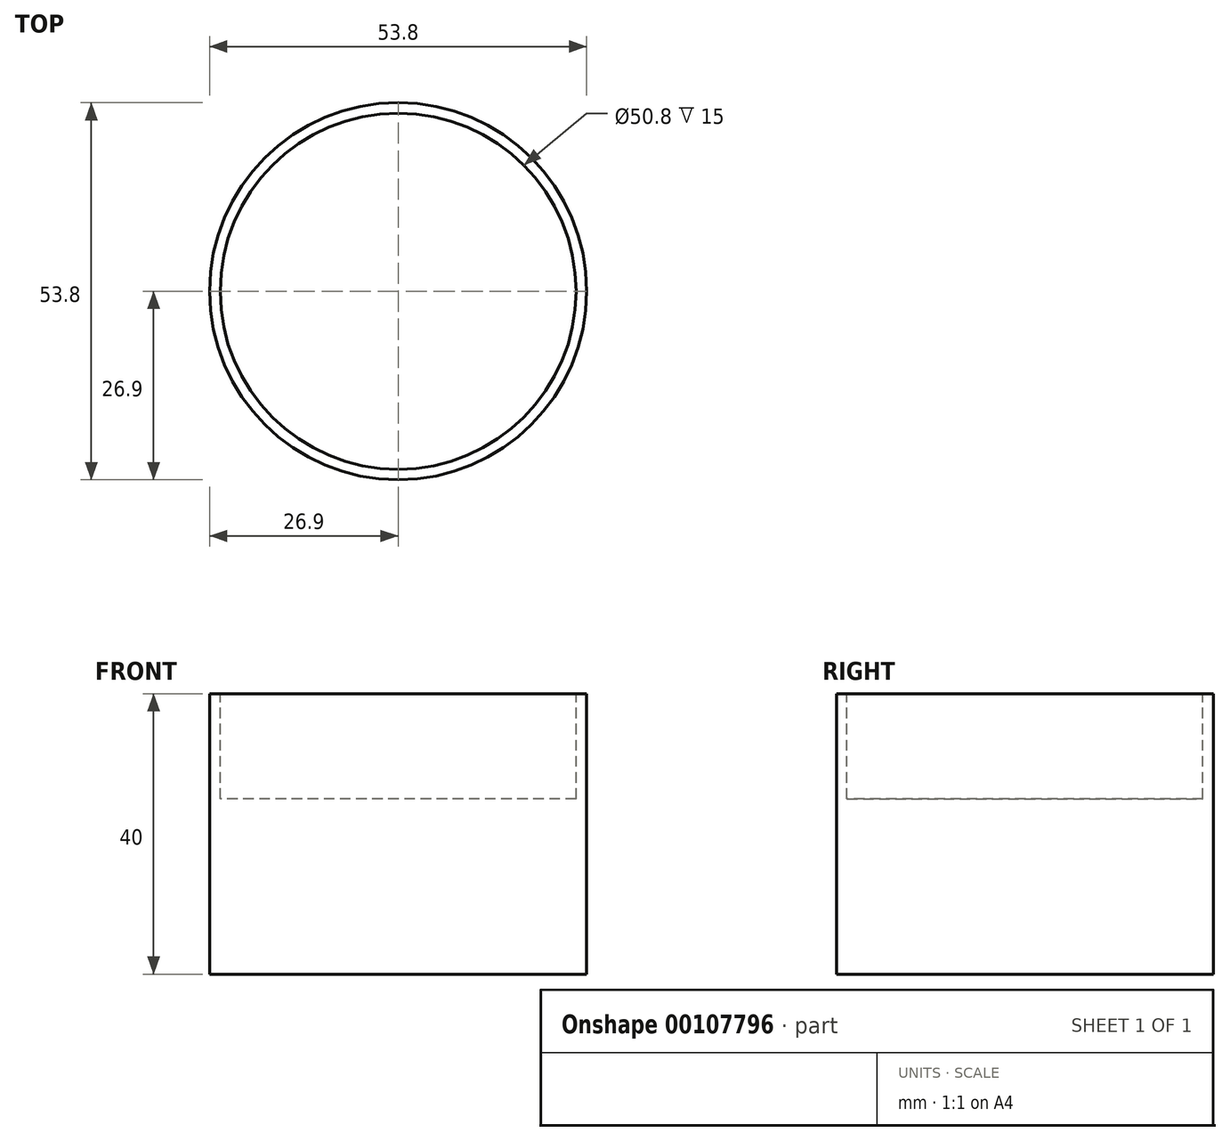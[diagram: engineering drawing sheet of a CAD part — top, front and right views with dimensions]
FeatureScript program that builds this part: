
annotation { "Feature Type Name" : "Feature", "Feature Type Description" : "" }
export const myFeature = defineFeature(function(context is Context, id is Id, definition is map)
    precondition{}
    {
        {
            var Q0;
            Q0=qCreatedBy(makeId("Top.planeOp"),FACE);
            var sketch = newSketch(context, id + "F0", { "sketchPlane" : qUnion([Q0])});
            skCircle(sketch, "E0", {"center": v(0, 0) * mm, "radius": 26.9 * mm});
            skSolve(sketch);
        }
        {
            var Q0;
            Q0=makeQuery(id+"F0.imprint","IMPRINT",FACE,{"disambiguationData":[TD([[makeQuery(id+"F0.imprint","IMPRINT",EDGE,{"derivedFrom":sQuery(id+"F0.wireOp",EDGE,"E0")}),1.0]])]});
            extrude(context, id + "F1", {"entities" : qUnion([Q0]), "depth" : 40 * mm});
        }
        {
            var Q0;
            Q0=makeQuery(id+"F1.opExtrude","CAP_FACE",FACE,{"disambiguationData":[OSD([sQuery(id+"F0.wireOp",EDGE,"E0")])],"isStart":false});
            var sketch = newSketch(context, id + "F2", { "sketchPlane" : qUnion([Q0])});
            skCircle(sketch, "E1", {"center": v(0, 0) * mm, "radius": 25.4 * mm});
            skCircle(sketch, "E2.0", {"center": v(0, 0) * mm, "radius": 26.9 * mm, "construction": true});
            skSolve(sketch);
        }
        {
            var Q0;
            Q0=makeQuery(id+"F2.imprint","IMPRINT",FACE,{"disambiguationData":[TD([[makeQuery(id+"F2.imprint","IMPRINT",EDGE,{"derivedFrom":sQuery(id+"F2.wireOp",EDGE,"E1")}),1.0]])]});
            extrude(context, id + "F3", {"entities" : qUnion([Q0]), "operationType" : NewBodyOperationType.REMOVE, "oppositeDirection" : true, "depth" : 15 * mm});
        }
    });
